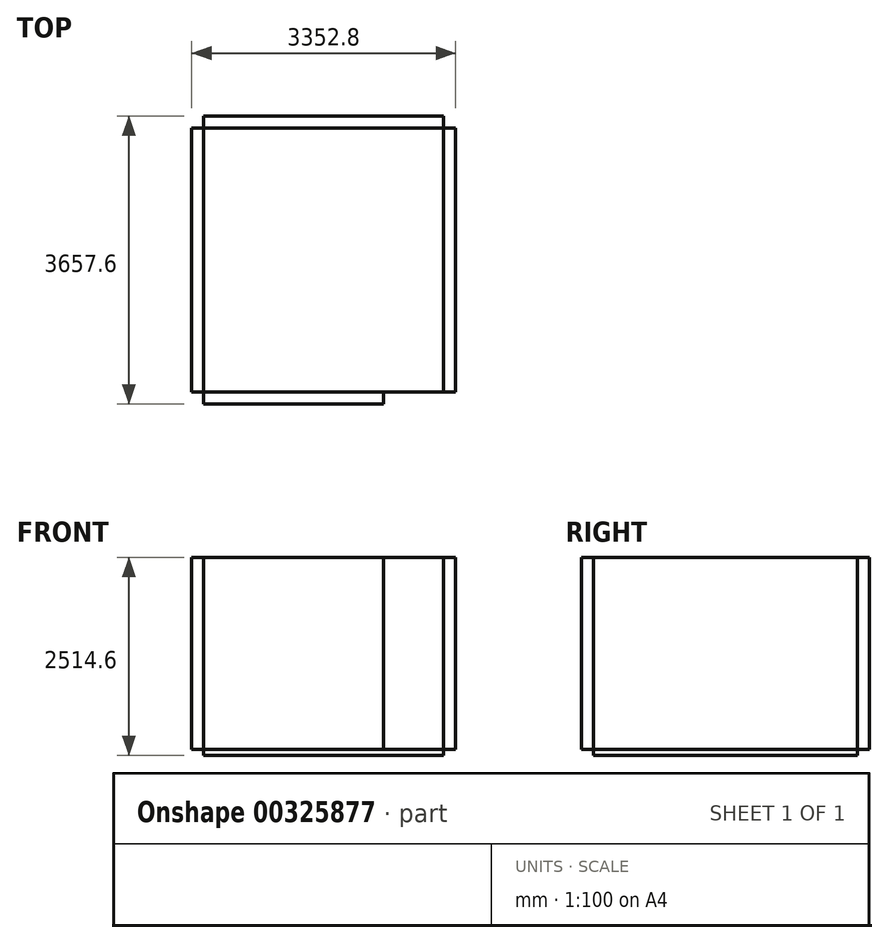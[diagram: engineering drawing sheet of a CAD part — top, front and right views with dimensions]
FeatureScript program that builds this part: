
annotation { "Feature Type Name" : "Feature", "Feature Type Description" : "" }
export const myFeature = defineFeature(function(context is Context, id is Id, definition is map)
    precondition{}
    {
        {
            var Q0;
            Q0=qCreatedBy(makeId("Top.planeOp"),FACE);
            var sketch = newSketch(context, id + "F0", { "sketchPlane" : qUnion([Q0])});
            skLineSegment(sketch, "E0.bottom", {"start": v(-1524, 1676.4) * mm, "end": v(1524, 1676.4) * mm});
            skLineSegment(sketch, "E0.top", {"start": v(-1524, -1676.4) * mm, "end": v(1524, -1676.4) * mm});
            skLineSegment(sketch, "E0.left", {"start": v(-1524, 1676.4) * mm, "end": v(-1524, -1676.4) * mm});
            skLineSegment(sketch, "E0.right", {"start": v(1524, 1676.4) * mm, "end": v(1524, -1676.4) * mm});
            skPoint(sketch, "E0.middle", {"position": v(0, 0) * mm});
            skLineSegment(sketch, "E1", {"start": v(1524, 1676.4) * mm, "end": v(1524, 1828.8) * mm});
            skLineSegment(sketch, "E2", {"start": v(1524, 1828.8) * mm, "end": v(-1524, 1828.8) * mm});
            skLineSegment(sketch, "E3", {"start": v(-1524, 1828.8) * mm, "end": v(-1524, 1676.4) * mm});
            skLineSegment(sketch, "E4", {"start": v(-1676.4, 1676.4) * mm, "end": v(-1676.4, -1676.4) * mm});
            skLineSegment(sketch, "E5", {"start": v(-1676.4, -1676.4) * mm, "end": v(-1524, -1676.4) * mm});
            skLineSegment(sketch, "E6", {"start": v(-1524, 1676.4) * mm, "end": v(-1676.4, 1676.4) * mm});
            skLineSegment(sketch, "E7", {"start": v(1524, 1676.4) * mm, "end": v(1676.4, 1676.4) * mm});
            skLineSegment(sketch, "E8", {"start": v(1676.4, 1676.4) * mm, "end": v(1676.4, -1676.4) * mm});
            skLineSegment(sketch, "E9", {"start": v(1676.4, -1676.4) * mm, "end": v(1524, -1676.4) * mm});
            skLineSegment(sketch, "E10", {"start": v(-1524, -1676.4) * mm, "end": v(-1524, -1828.8) * mm});
            skLineSegment(sketch, "E11", {"start": v(-1524, -1828.8) * mm, "end": v(762, -1828.8) * mm});
            skLineSegment(sketch, "E12", {"start": v(762, -1828.8) * mm, "end": v(762, -1676.4) * mm});
            skSolve(sketch);
        }
        {
            var Q0;
            Q0=makeQuery(id+"F0.imprint","IMPRINT",FACE,{"disambiguationData":[TD([[makeQuery(id+"F0.imprint","IMPRINT",EDGE,{"derivedFrom":sQuery(id+"F0.wireOp",EDGE,"E0.bottom")}),1.0]])]});
            var Q1;
            {var subQ0=sQuery(id+"F0.wireOp",EDGE,"E10");Q1=makeQuery(id+"F0.imprint","IMPRINT",FACE,{"disambiguationData":[TD([[makeQuery(id+"F0.imprint","IMPRINT",EDGE,{"derivedFrom":subQ0}),1.0]])]});}
            var Q2;
            Q2=makeQuery(id+"F0.imprint","IMPRINT",FACE,{"disambiguationData":[TD([[makeQuery(id+"F0.imprint","IMPRINT",EDGE,{"derivedFrom":sQuery(id+"F0.wireOp",EDGE,"E0.right")}),1.0]])]});
            var Q3;
            Q3=makeQuery(id+"F0.imprint","IMPRINT",FACE,{"disambiguationData":[TD([[makeQuery(id+"F0.imprint","IMPRINT",EDGE,{"derivedFrom":sQuery(id+"F0.wireOp",EDGE,"E0.left")}),-1.0]])]});
            extrude(context, id + "F1", {"entities" : qUnion([Q0, Q1, Q2, Q3]), "depth" : 2438.4 * mm});
        }
        {
            var Q0;
            Q0=makeQuery(id+"F1.opExtrude","CAP_FACE",FACE,{"disambiguationData":[OSD([sQuery(id+"F0.wireOp",EDGE,"E0.left"),sQuery(id+"F0.wireOp",EDGE,"E4"),sQuery(id+"F0.wireOp",EDGE,"E5"),sQuery(id+"F0.wireOp",EDGE,"E6")])],"isStart":true});
            var sketch = newSketch(context, id + "F2", { "sketchPlane" : qUnion([Q0])});
            skLineSegment(sketch, "E13.bottom", {"start": v(-1524, 1676.4) * mm, "end": v(1524, 1676.4) * mm});
            skLineSegment(sketch, "E13.top", {"start": v(-1524, -1676.4) * mm, "end": v(1524, -1676.4) * mm});
            skLineSegment(sketch, "E13.left", {"start": v(-1524, 1676.4) * mm, "end": v(-1524, -1676.4) * mm});
            skLineSegment(sketch, "E13.right", {"start": v(1524, 1676.4) * mm, "end": v(1524, -1676.4) * mm});
            skSolve(sketch);
        }
        {
            var Q0;
            Q0=makeQuery(id+"F2.imprint","IMPRINT",FACE,{"disambiguationData":[TD([[makeQuery(id+"F2.imprint","IMPRINT",EDGE,{"derivedFrom":sQuery(id+"F2.wireOp",EDGE,"E13.bottom")}),-1.0]])]});
            extrude(context, id + "F3", {"entities" : qUnion([Q0]), "depth" : 76.2 * mm});
        }
    });
